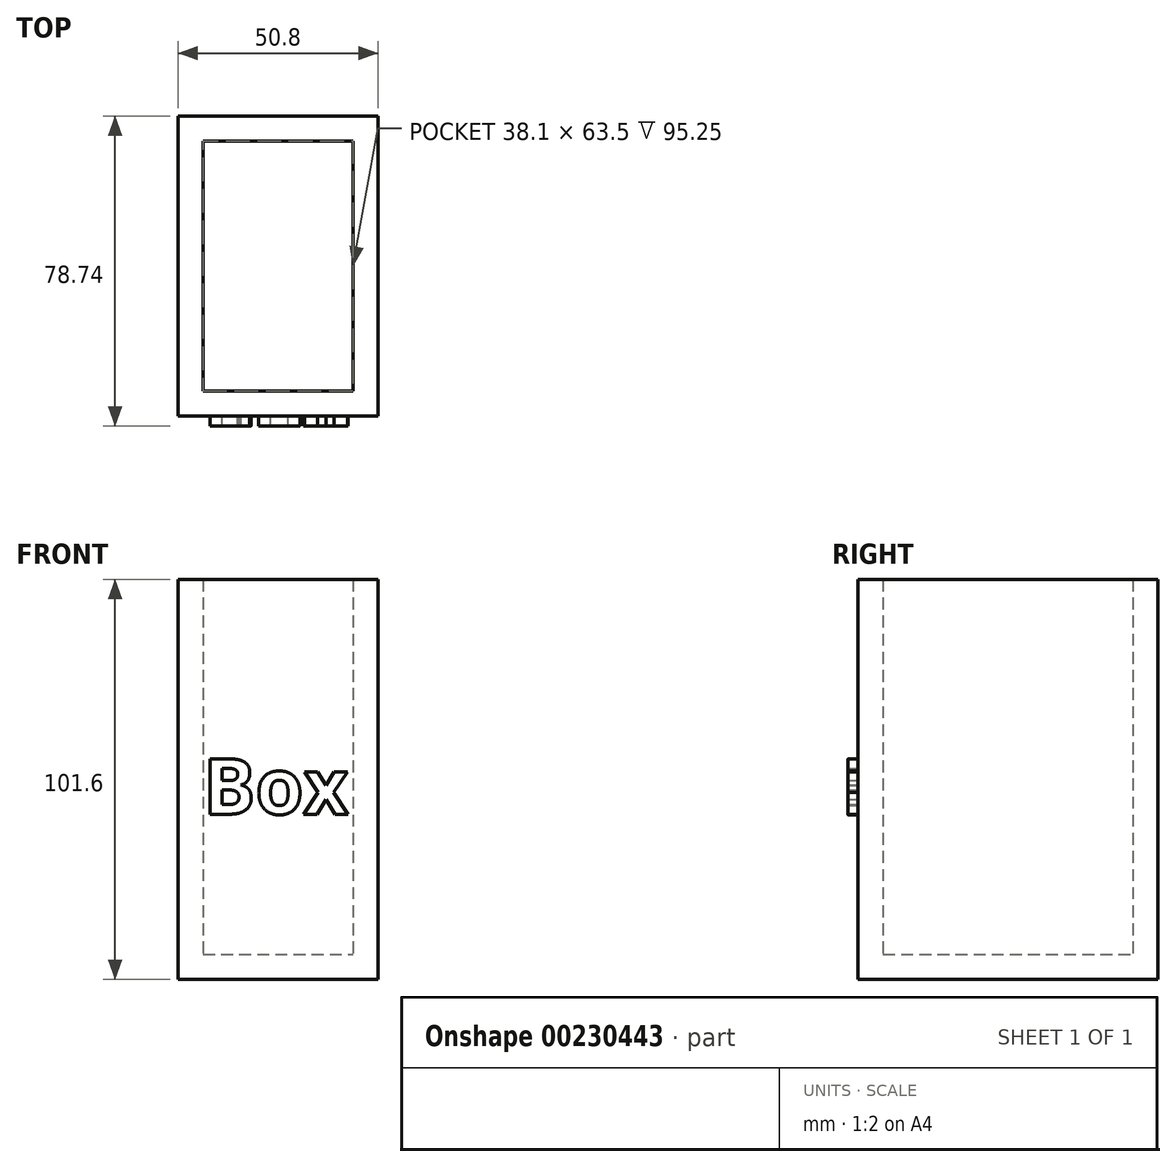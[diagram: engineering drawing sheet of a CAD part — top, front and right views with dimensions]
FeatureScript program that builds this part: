
annotation { "Feature Type Name" : "Feature", "Feature Type Description" : "" }
export const myFeature = defineFeature(function(context is Context, id is Id, definition is map)
    precondition{}
    {
        {
            var Q0;
            Q0=qCreatedBy(makeId("Front.planeOp"),FACE);
            var sketch = newSketch(context, id + "F0", { "sketchPlane" : qUnion([Q0])});
            skLineSegment(sketch, "E0.bottom", {"start": v(-49.65, 77.4) * mm, "end": v(1.15, 77.4) * mm});
            skLineSegment(sketch, "E0.top", {"start": v(-49.65, -24.2) * mm, "end": v(1.15, -24.2) * mm});
            skLineSegment(sketch, "E0.left", {"start": v(-49.65, 77.4) * mm, "end": v(-49.65, -24.2) * mm});
            skLineSegment(sketch, "E0.right", {"start": v(1.15, 77.4) * mm, "end": v(1.15, -24.2) * mm});
            skSolve(sketch);
        }
        {
            var Q0;
            Q0 = qSketchRegion(id + "F0", true);
            extrude(context, id + "F1", {"entities" : qUnion([Q0]), "depth" : 76.2 * mm});
        }
        {
            var Q0;
            Q0=makeQuery(id+"F1.opExtrude","SWEPT_FACE",FACE,{"disambiguationData":[OSD([sQuery(id+"F0.wireOp",EDGE,"E0.bottom")])]});
            shell(context, id + "F2", {"entities" : qUnion([Q0]), "thickness" : 6.35 * mm});
        }
        {
            var Q0;
            Q0=makeQuery(id+"F1.opExtrude","CAP_FACE",FACE,{"disambiguationData":[OSD([sQuery(id+"F0.wireOp",EDGE,"E0.bottom"),sQuery(id+"F0.wireOp",EDGE,"E0.top"),sQuery(id+"F0.wireOp",EDGE,"E0.left"),sQuery(id+"F0.wireOp",EDGE,"E0.right")])],"isStart":false});
            var sketch = newSketch(context, id + "F3", { "sketchPlane" : qUnion([Q0])});
            skText(sketch, "E1", { "text": "Box", "fontName": "OpenSans-Bold.ttf"});
            const initialGuessF3  = {"E1": [-0.0433, 0.01778, 1, 0, 0.01422]};
            skSetInitialGuess(sketch, initialGuessF3);
            skSolve(sketch);
        }
        {
            var Q0;
            Q0 = qSketchRegion(id + "F3", true);
            extrude(context, id + "F4", {"entities" : qUnion([Q0]), "operationType" : NewBodyOperationType.ADD, "depth" : 2.54 * mm});
        }
    });
